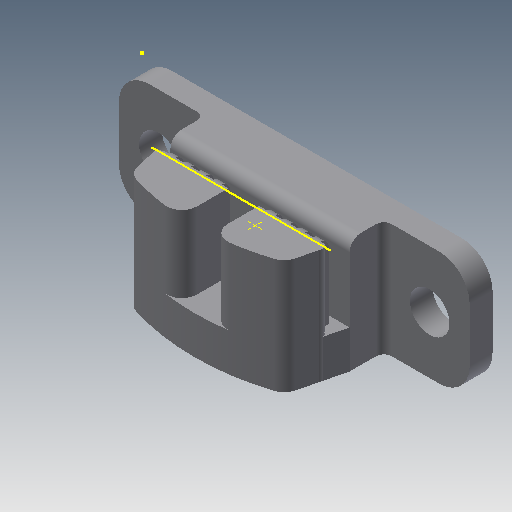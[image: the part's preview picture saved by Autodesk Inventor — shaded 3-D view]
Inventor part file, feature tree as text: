
AUTODESK INVENTOR PART (.ipt)
format: ipt  version: 2017 (Build 210142000, 142)  size: 601,088 bytes
history: native  units: mm
features: sketch x13, extrude x10, projected_geometry x10, fillet x2, direct_edit x1, move_body x1
ambient origin geometry x8: Origin, YZ Plane, XZ Plane, XY Plane, X Axis, Y Axis, Z Axis, Center Point
bodies: Solid1 (feature_tree)
feature tree (37):
  extrude  "Extrusion1"  Depth=15.0mm
  extrude  "Extrusion2"  Depth=15.0mm TaperAngle=0.0deg
  sketch  "Sketch3"  dims[d10=7.25mm d11=90.0deg]
  sketch  "Sketch4"  dims[d12=12.0mm d13=0.0mm d14=10.0mm]
  extrude  "Extrusion3"  TaperAngle=90.0deg  [1 undecoded]
  extrude  "Extrusion4"  Depth=10.0mm
  sketch  "Sketch6"  dims[d21=1.0mm d22=1.2mm d23=1.0mm d24=1.0mm d25=1.0mm d26=1.0mm d27=1.2mm d28=1.0mm d29=1.0mm]
  extrude  "Extrusion5"  Depth=1.0mm
  extrude  "Extrusion6"  Depth=0.75mm
  extrude  "Extrusion7"  Depth=15.0mm TaperAngle=0.0deg
  extrude  "Extrusion8"  Depth=10.0mm TaperAngle=0.0deg
  fillet  "Fillet1"  Radius=10.0mm
  extrude  "Extrusion9"  Depth=1.5mm
  extrude  "Extrusion10"  Depth=1.0mm
  fillet  "Fillet2"  Radius=7.0mm
  sketch  "Sketch13"  dims[d70=2.75mm d71=0.0mm d72=90.0deg d73=90.0deg d74=10.0mm d75=0.0mm d76=2.0mm d77=0.0mm d78=0.0mm d79=-2.5mm]
  direct_edit  "Direct Edit1"
  sketch  "Sketch1"  dims[d0=46.0mm d1=15.0mm]
  sketch  "Sketch2"  dims[d6=4.0mm d7=15.0mm d8=0.0mm]
  projected_geometry  "Projected Loop1"
  sketch  "Sketch5"  dims[d20=1.0mm]
  projected_geometry  "Projected Loop2"
  projected_geometry  "Projected Loop3"
  projected_geometry  "Projected Loop4"
  sketch  "Sketch7"  dims[d34=1.0mm d35=1.0mm d36=1.0mm d37=1.2mm d38=1.0mm d39=1.0mm d40=1.0mm d41=1.0mm d42=1.2mm d43=1.0mm d52=0.75mm]
  projected_geometry  "Projected Loop5"
  projected_geometry  "Projected Loop6"
  sketch  "Sketch8"  dims[d53=2.0mm d54=0.0mm d55=15.0mm d56=0.0mm]
  projected_geometry  "Projected Loop7"
  projected_geometry  "Projected Loop8"
  sketch  "Sketch9"  dims[d57=0.9mm d58=10.0mm d59=0.0mm d60=10.0mm d61=0.0mm]
  projected_geometry  "Projected Loop9"
  sketch  "Sketch10"  dims[d62=10.0mm d63=0.0mm d64=1.5mm]
  sketch  "Sketch11"  dims[d65=10.0mm d66=0.0mm d67=1.0mm d68=7.0mm]
  sketch  "Sketch12"  dims[d69=2.0mm]
  projected_geometry  "Projected Loop10"
  move_body  "Move1"
note: 1 required parameter value undecoded (feature->parameter linkage not recoverable at this tier; creation-order binding heuristic only, values carry confidence <= 0.55)
